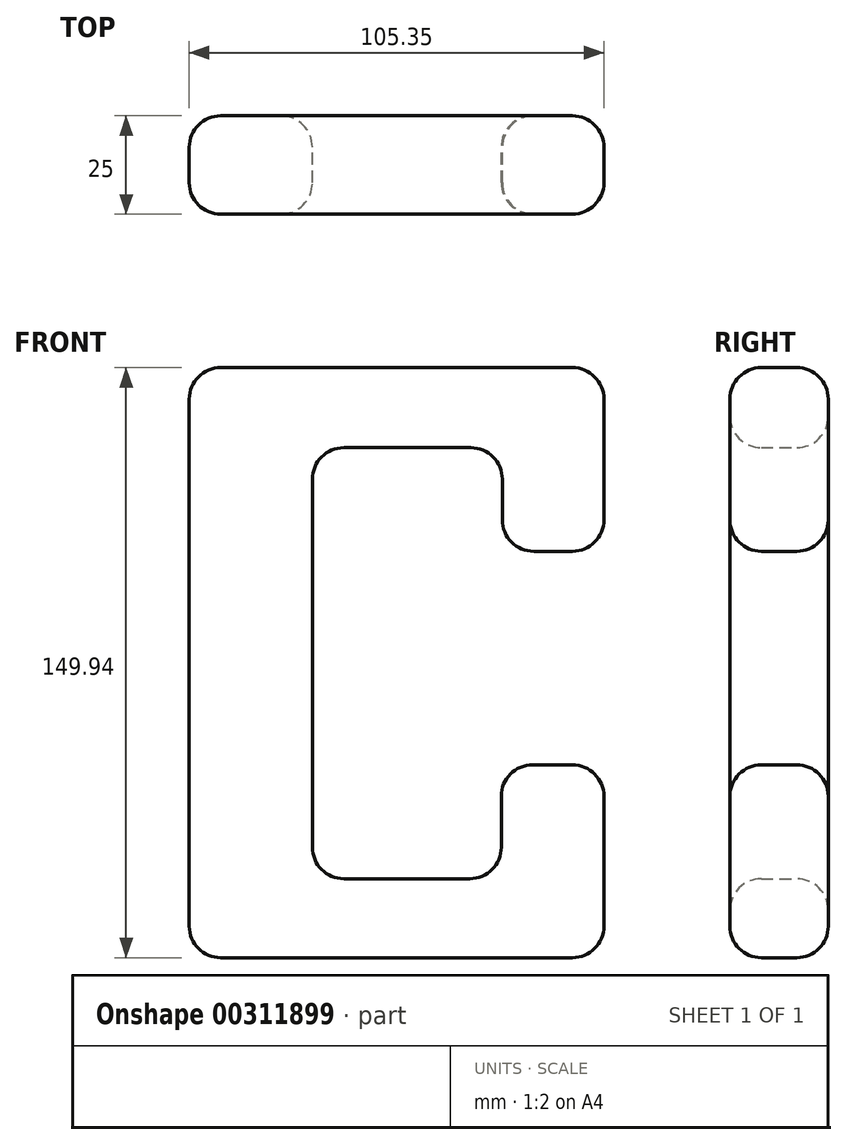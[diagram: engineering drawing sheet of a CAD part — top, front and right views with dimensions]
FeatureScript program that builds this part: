
annotation { "Feature Type Name" : "Feature", "Feature Type Description" : "" }
export const myFeature = defineFeature(function(context is Context, id is Id, definition is map)
    precondition{}
    {
        {
            var Q0;
            Q0=qCreatedBy(makeId("Front.planeOp"),FACE);
            var sketch = newSketch(context, id + "F0", { "sketchPlane" : qUnion([Q0])});
            skLineSegment(sketch, "E0.bottom", {"start": v(-50.07, 75.1) * mm, "end": v(-18.77, 75.1) * mm});
            skLineSegment(sketch, "E0.top", {"start": v(-50.07, -74.84) * mm, "end": v(-18.77, -74.84) * mm});
            skLineSegment(sketch, "E0.left", {"start": v(-50.07, 75.1) * mm, "end": v(-50.07, -74.84) * mm});
            skLineSegment(sketch, "E0.right", {"start": v(-18.77, 54.76) * mm, "end": v(-18.77, -54.76) * mm});
            skLineSegment(sketch, "E1.bottom", {"start": v(-18.77, -74.84) * mm, "end": v(55.28, -74.84) * mm});
            skLineSegment(sketch, "E1.top", {"start": v(-18.77, -54.76) * mm, "end": v(29.2, -54.76) * mm});
            skLineSegment(sketch, "E1.right", {"start": v(55.28, -74.84) * mm, "end": v(55.28, -54.76) * mm});
            skLineSegment(sketch, "E2.top", {"start": v(55.28, -25.82) * mm, "end": v(29.2, -25.82) * mm});
            skLineSegment(sketch, "E2.left", {"start": v(55.28, -54.76) * mm, "end": v(55.28, -25.82) * mm});
            skLineSegment(sketch, "E2.right", {"start": v(29.2, -54.76) * mm, "end": v(29.2, -25.82) * mm});
            skLineSegment(sketch, "E3.bottom", {"start": v(-18.77, 75.1) * mm, "end": v(55.28, 75.1) * mm});
            skLineSegment(sketch, "E3.top", {"start": v(-18.77, 54.76) * mm, "end": v(29.47, 54.76) * mm});
            skLineSegment(sketch, "E3.right", {"start": v(55.28, 75.1) * mm, "end": v(55.28, 54.76) * mm});
            skLineSegment(sketch, "E4.top", {"start": v(55.28, 28.42) * mm, "end": v(29.47, 28.42) * mm});
            skLineSegment(sketch, "E4.left", {"start": v(55.28, 54.76) * mm, "end": v(55.28, 28.42) * mm});
            skLineSegment(sketch, "E4.right", {"start": v(29.47, 54.76) * mm, "end": v(29.47, 28.42) * mm});
            skSolve(sketch);
        }
        {
            var Q0;
            Q0=makeQuery(id+"F0.imprint","IMPRINT",FACE,{"disambiguationData":[TD([[makeQuery(id+"F0.imprint","IMPRINT",EDGE,{"derivedFrom":sQuery(id+"F0.wireOp",EDGE,"E0.bottom")}),-1.0]])]});
            extrude(context, id + "F1", {"entities" : qUnion([Q0]), "depth" : 25 * mm});
        }
        {
            var Q0;
            Q0=makeQuery(id+"F1.opExtrude","CAP_FACE",FACE,{"disambiguationData":[OSD([sQuery(id+"F0.wireOp",EDGE,"E0.bottom"),sQuery(id+"F0.wireOp",EDGE,"E0.top"),sQuery(id+"F0.wireOp",EDGE,"E0.left"),sQuery(id+"F0.wireOp",EDGE,"E0.right"),sQuery(id+"F0.wireOp",EDGE,"E1.bottom"),sQuery(id+"F0.wireOp",EDGE,"E1.top"),sQuery(id+"F0.wireOp",EDGE,"E1.right"),sQuery(id+"F0.wireOp",EDGE,"E2.top"),sQuery(id+"F0.wireOp",EDGE,"E2.left"),sQuery(id+"F0.wireOp",EDGE,"E2.right"),sQuery(id+"F0.wireOp",EDGE,"E3.bottom"),sQuery(id+"F0.wireOp",EDGE,"E3.top"),sQuery(id+"F0.wireOp",EDGE,"E3.right"),sQuery(id+"F0.wireOp",EDGE,"E4.top"),sQuery(id+"F0.wireOp",EDGE,"E4.left"),sQuery(id+"F0.wireOp",EDGE,"E4.right")])],"isStart":false});
            var Q1;
            Q1=makeQuery(id+"F1.opExtrude","SWEPT_EDGE",EDGE,{"disambiguationData":[OSD([sQuery(id+"F0.wireOp",EDGE,"E0.right"),sQuery(id+"F0.wireOp",EDGE,"E1.top")])]});
            var Q2;
            Q2=makeQuery(id+"F1.opExtrude","SWEPT_EDGE",EDGE,{"disambiguationData":[OSD([sQuery(id+"F0.wireOp",EDGE,"E1.top"),sQuery(id+"F0.wireOp",EDGE,"E2.right")])]});
            var Q3;
            Q3=makeQuery(id+"F1.opExtrude","SWEPT_EDGE",EDGE,{"disambiguationData":[OSD([sQuery(id+"F0.wireOp",EDGE,"E3.top"),sQuery(id+"F0.wireOp",EDGE,"E4.right")])]});
            var Q4;
            Q4=makeQuery(id+"F1.opExtrude","SWEPT_EDGE",EDGE,{"disambiguationData":[OSD([sQuery(id+"F0.wireOp",EDGE,"E0.right"),sQuery(id+"F0.wireOp",EDGE,"E3.top")])]});
            var Q5;
            Q5=makeQuery(id+"F1.opExtrude","SWEPT_EDGE",EDGE,{"disambiguationData":[OSD([sQuery(id+"F0.wireOp",EDGE,"E4.top"),sQuery(id+"F0.wireOp",EDGE,"E4.left")])]});
            var Q6;
            Q6=makeQuery(id+"F1.opExtrude","SWEPT_EDGE",EDGE,{"disambiguationData":[OSD([sQuery(id+"F0.wireOp",EDGE,"E4.top"),sQuery(id+"F0.wireOp",EDGE,"E4.right")])]});
            var Q7;
            Q7=makeQuery(id+"F1.opExtrude","SWEPT_EDGE",EDGE,{"disambiguationData":[OSD([sQuery(id+"F0.wireOp",EDGE,"E3.bottom"),sQuery(id+"F0.wireOp",EDGE,"E3.right")])]});
            var Q8;
            Q8=makeQuery(id+"F1.opExtrude","SWEPT_EDGE",EDGE,{"disambiguationData":[OSD([sQuery(id+"F0.wireOp",EDGE,"E2.top"),sQuery(id+"F0.wireOp",EDGE,"E2.left")])]});
            var Q9;
            Q9=makeQuery(id+"F1.opExtrude","SWEPT_EDGE",EDGE,{"disambiguationData":[OSD([sQuery(id+"F0.wireOp",EDGE,"E2.top"),sQuery(id+"F0.wireOp",EDGE,"E2.right")])]});
            var Q10;
            Q10=makeQuery(id+"F1.opExtrude","SWEPT_EDGE",EDGE,{"disambiguationData":[OSD([sQuery(id+"F0.wireOp",EDGE,"E1.bottom"),sQuery(id+"F0.wireOp",EDGE,"E1.right")])]});
            var Q11;
            Q11=makeQuery(id+"F1.opExtrude","SWEPT_EDGE",EDGE,{"disambiguationData":[OSD([sQuery(id+"F0.wireOp",EDGE,"E0.top"),sQuery(id+"F0.wireOp",EDGE,"E0.left")])]});
            var Q12;
            Q12=makeQuery(id+"F1.opExtrude","SWEPT_EDGE",EDGE,{"disambiguationData":[OSD([sQuery(id+"F0.wireOp",EDGE,"E0.bottom"),sQuery(id+"F0.wireOp",EDGE,"E0.left")])]});
            var Q13;
            Q13=makeQuery(id+"F1.opExtrude","CAP_FACE",FACE,{"disambiguationData":[OSD([sQuery(id+"F0.wireOp",EDGE,"E0.bottom"),sQuery(id+"F0.wireOp",EDGE,"E0.top"),sQuery(id+"F0.wireOp",EDGE,"E0.left"),sQuery(id+"F0.wireOp",EDGE,"E0.right"),sQuery(id+"F0.wireOp",EDGE,"E1.bottom"),sQuery(id+"F0.wireOp",EDGE,"E1.top"),sQuery(id+"F0.wireOp",EDGE,"E1.right"),sQuery(id+"F0.wireOp",EDGE,"E2.top"),sQuery(id+"F0.wireOp",EDGE,"E2.left"),sQuery(id+"F0.wireOp",EDGE,"E2.right"),sQuery(id+"F0.wireOp",EDGE,"E3.bottom"),sQuery(id+"F0.wireOp",EDGE,"E3.top"),sQuery(id+"F0.wireOp",EDGE,"E3.right"),sQuery(id+"F0.wireOp",EDGE,"E4.top"),sQuery(id+"F0.wireOp",EDGE,"E4.left"),sQuery(id+"F0.wireOp",EDGE,"E4.right")])],"isStart":true});
            fillet(context, id + "F2", {"entities" : qUnion([Q0, Q1, Q2, Q3, Q4, Q5, Q6, Q7, Q8, Q9, Q10, Q11, Q12, Q13]), "radius" : 8 * mm, "tangentPropagation" : true, "allowEdgeOverflow" : false});
        }
    });
